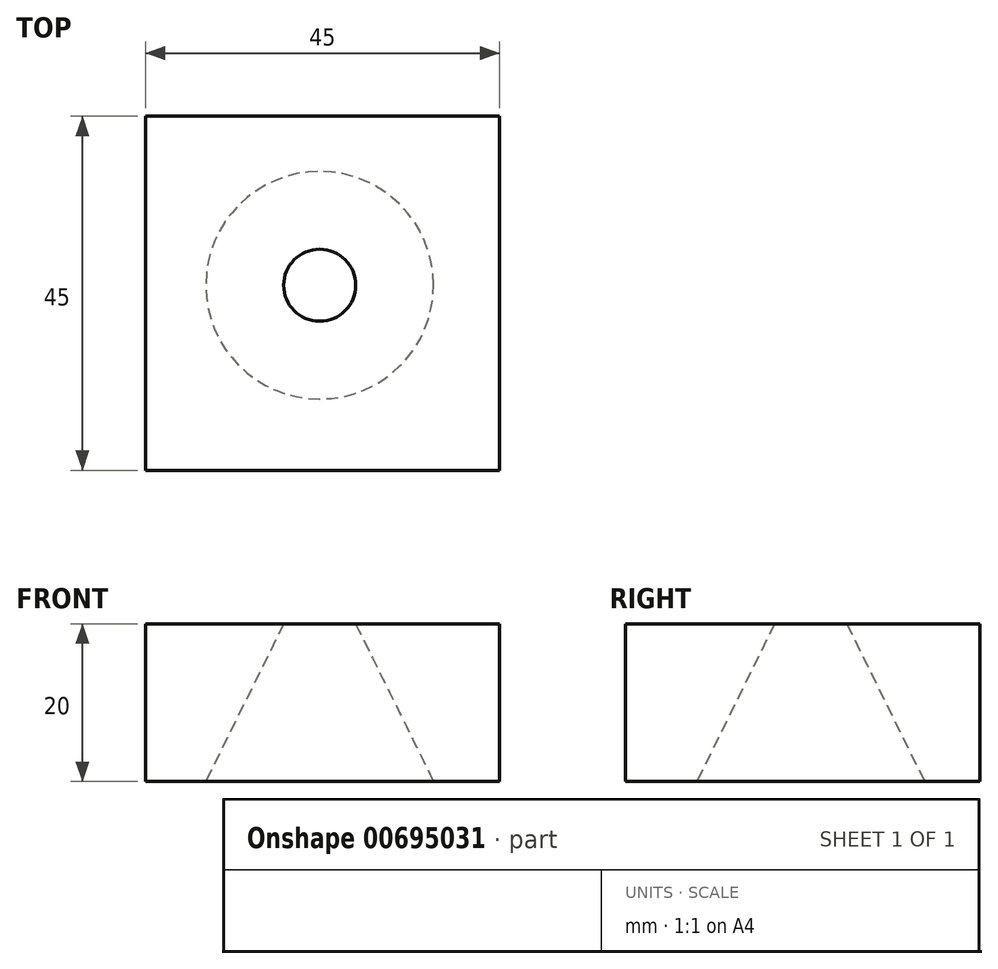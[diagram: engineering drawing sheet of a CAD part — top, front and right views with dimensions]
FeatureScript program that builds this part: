
annotation { "Feature Type Name" : "Feature", "Feature Type Description" : "" }
export const myFeature = defineFeature(function(context is Context, id is Id, definition is map)
    precondition{}
    {
        {
            var Q0;
            Q0=qCreatedBy(makeId("Top.planeOp"),FACE);
            var sketch = newSketch(context, id + "F0", { "sketchPlane" : qUnion([Q0])});
            skLineSegment(sketch, "E0.bottom", {"start": v(0, 0) * mm, "end": v(45, 0) * mm});
            skLineSegment(sketch, "E0.top", {"start": v(0, 45) * mm, "end": v(45, 45) * mm});
            skLineSegment(sketch, "E0.left", {"start": v(0, 0) * mm, "end": v(0, 45) * mm});
            skLineSegment(sketch, "E0.right", {"start": v(45, 0) * mm, "end": v(45, 45) * mm});
            skSolve(sketch);
        }
        {
            var Q0;
            Q0=makeQuery(id+"F0.imprint","IMPRINT",FACE,{"disambiguationData":[TD([[makeQuery(id+"F0.imprint","IMPRINT",EDGE,{"derivedFrom":sQuery(id+"F0.wireOp",EDGE,"E0.bottom")}),1.0]])]});
            extrude(context, id + "F1", {"entities" : qUnion([Q0]), "depth" : 20 * mm, "offsetDistance" : 25 * mm});
        }
        {
            var Q0;
            Q0=makeQuery(id+"F1.opExtrude","CAP_FACE",FACE,{"disambiguationData":[OSD([sQuery(id+"F0.wireOp",EDGE,"E0.bottom"),sQuery(id+"F0.wireOp",EDGE,"E0.top"),sQuery(id+"F0.wireOp",EDGE,"E0.left"),sQuery(id+"F0.wireOp",EDGE,"E0.right")])],"isStart":false});
            var sketch = newSketch(context, id + "F2", { "sketchPlane" : qUnion([Q0])});
            skCircle(sketch, "E1", {"center": v(22.15, 23.52) * mm, "radius": 4.58 * mm});
            skSolve(sketch);
        }
        {
            var Q0;
            Q0=makeQuery(id+"F2.imprint","IMPRINT",FACE,{"disambiguationData":[TD([[makeQuery(id+"F2.imprint","IMPRINT",EDGE,{"derivedFrom":sQuery(id+"F2.wireOp",EDGE,"E1")}),1.0]])]});
            extrude(context, id + "F3", {"entities" : qUnion([Q0]), "operationType" : NewBodyOperationType.REMOVE, "oppositeDirection" : true, "depth" : 25 * mm, "offsetDistance" : 25 * mm, "hasDraft" : true, "draftAngle" : 26.3 * degree});
        }
    });
